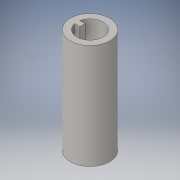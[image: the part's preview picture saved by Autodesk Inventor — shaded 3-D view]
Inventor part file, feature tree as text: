
AUTODESK INVENTOR PART (.ipt)
format: ipt  version: 2016 (Build 200138000, 138)  size: 96,768 bytes
history: native  units: in
note: dims shown in document units (in); Inventor stores cm internally (conversion verified against a paired STEP export)
features: extrude x1, sketch x1
ambient origin geometry x8: Origin, YZ Plane, XZ Plane, XY Plane, X Axis, Y Axis, Z Axis, Center Point
bodies: Solid1 (feature_tree)
feature tree (2):
  extrude  "Extrusion1"  Depth=2.0in
  sketch  "Sketch1"  dims[d0=0.75in d1=0.5in d3=0.1in d4=0.1in d5=2.0in d6=0.0in]
